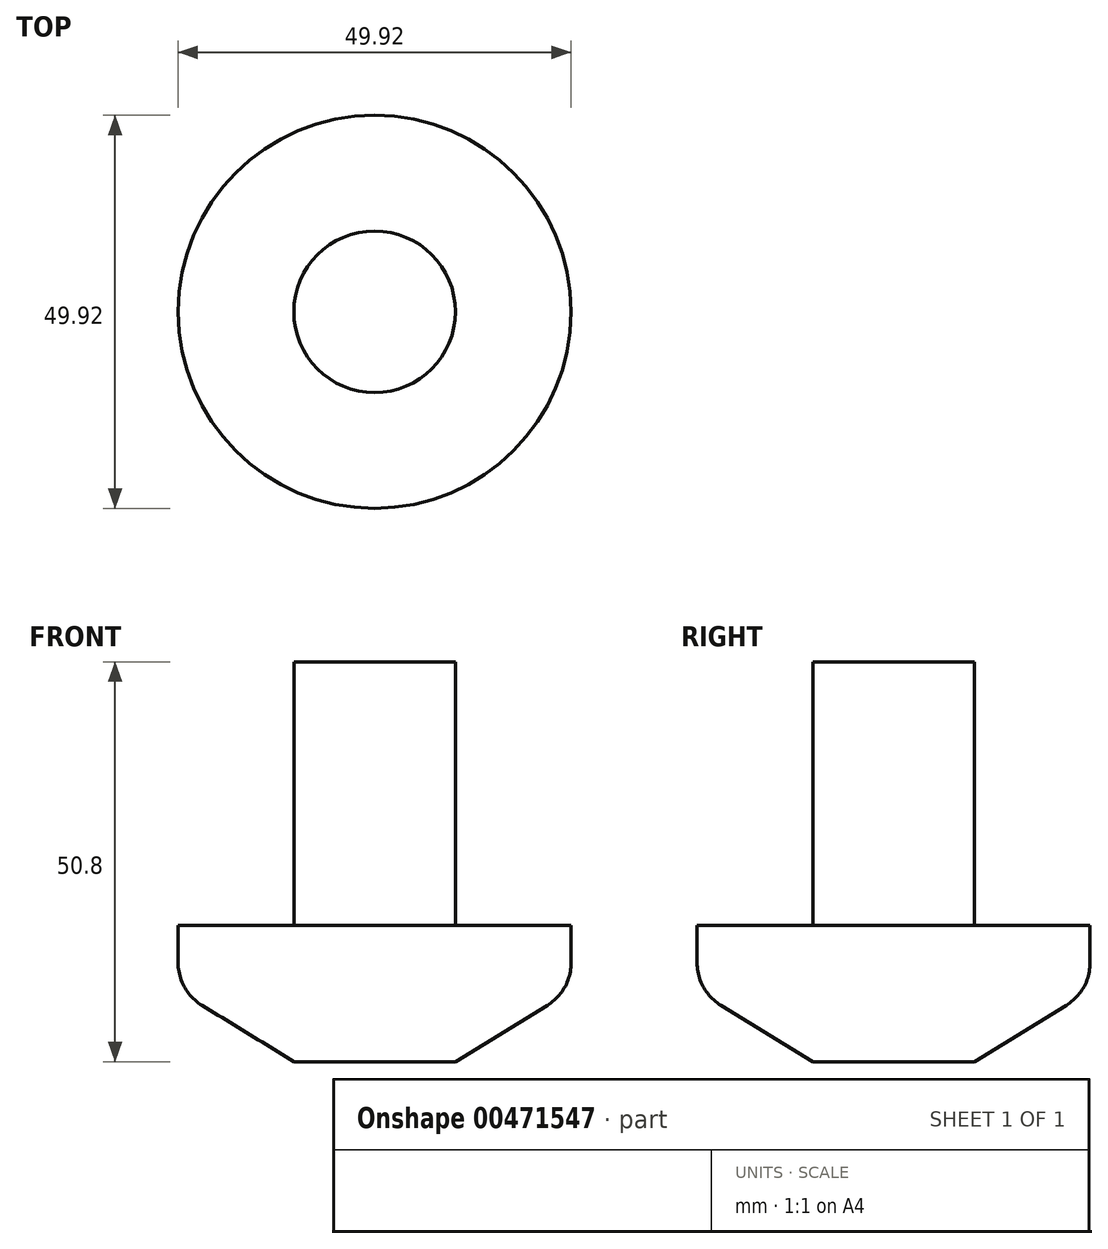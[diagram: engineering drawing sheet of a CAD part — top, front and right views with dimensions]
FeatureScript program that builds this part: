
annotation { "Feature Type Name" : "Feature", "Feature Type Description" : "" }
export const myFeature = defineFeature(function(context is Context, id is Id, definition is map)
    precondition{}
    {
        {
            var Q0;
            Q0=qCreatedBy(makeId("Front.planeOp"),FACE);
            var sketch = newSketch(context, id + "F0", { "sketchPlane" : qUnion([Q0])});
            skLineSegment(sketch, "E0", {"start": v(0, 0) * mm, "end": v(0, 50.8) * mm});
            skLineSegment(sketch, "E1", {"start": v(0, 0) * mm, "end": v(10.26, 0) * mm});
            skLineSegment(sketch, "E2", {"start": v(10.26, 0) * mm, "end": v(21.93, 7.15) * mm});
            skLineSegment(sketch, "E3", {"start": v(24.96, 12.57) * mm, "end": v(24.96, 17.33) * mm});
            skLineSegment(sketch, "E4", {"start": v(24.96, 17.33) * mm, "end": v(10.26, 17.33) * mm});
            skLineSegment(sketch, "E5", {"start": v(10.26, 17.33) * mm, "end": v(10.26, 50.8) * mm});
            skLineSegment(sketch, "E6", {"start": v(10.26, 50.8) * mm, "end": v(0, 50.8) * mm});
            skPoint(sketch, "E7.visualSharp", {"position": v(24.96, 9.01) * mm});
            skArc(sketch, "E7.filletArc", {"start": v(21.93, 7.15) * mm, "mid": v(24.15, 9.47) * mm, "end": v(24.96, 12.57) * mm});
            skSolve(sketch);
        }
        {
            var Q0;
            Q0=makeQuery(id+"F0.imprint","IMPRINT",FACE,{"disambiguationData":[TD([[makeQuery(id+"F0.imprint","IMPRINT",EDGE,{"derivedFrom":sQuery(id+"F0.wireOp",EDGE,"E0")}),-1.0]])]});
            var Q1;
            Q1=sQuery(id+"F0.wireOp",EDGE,"E0");
            revolve(context, id + "F1", {"entities" : qUnion([Q0]), "axis" : qUnion([Q1]), "revolveType" : RevolveType.FULL});
        }
    });
